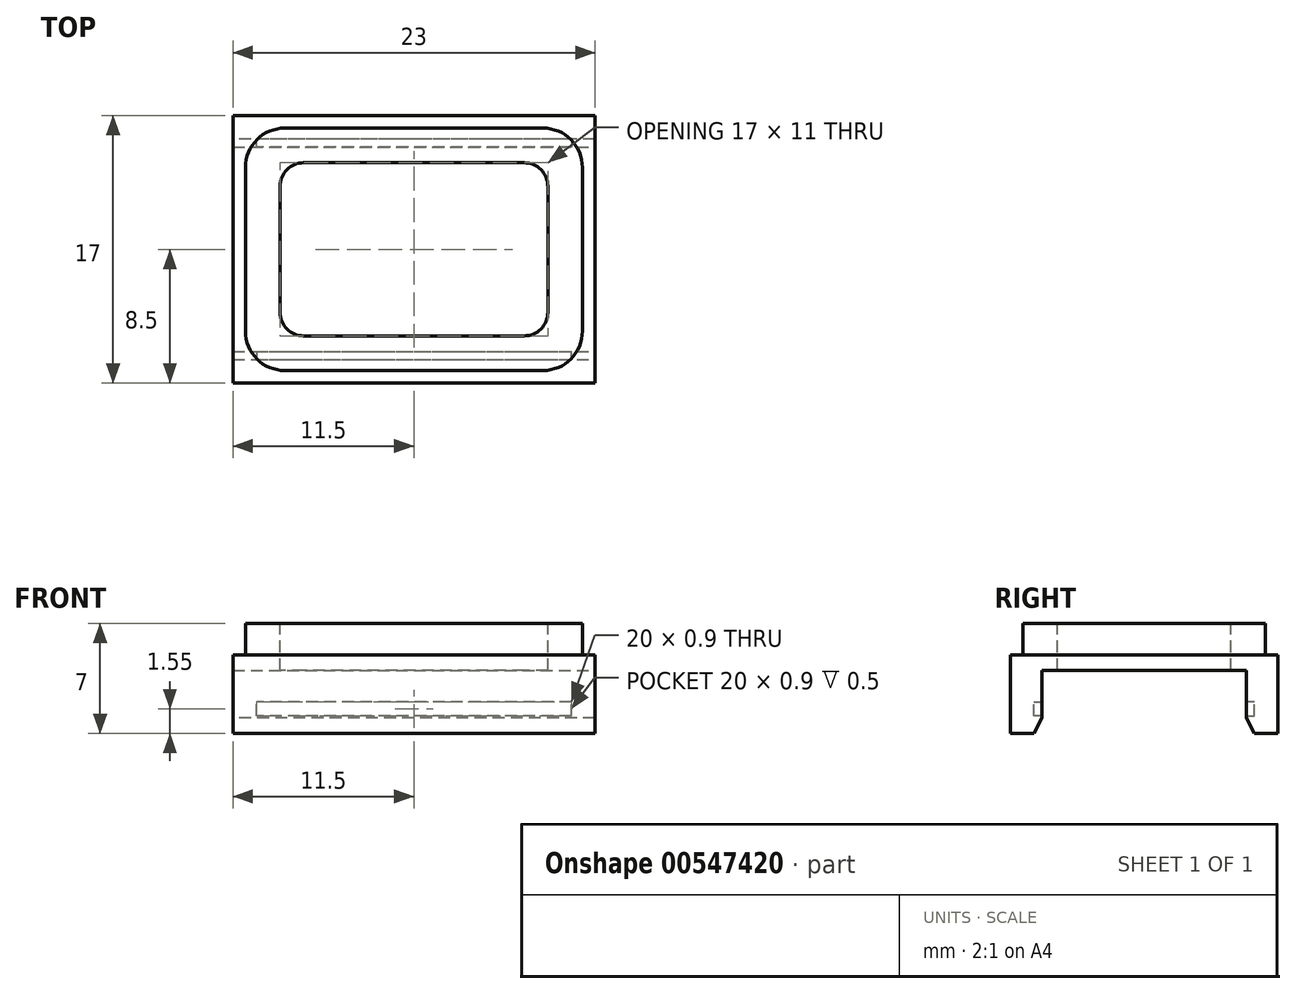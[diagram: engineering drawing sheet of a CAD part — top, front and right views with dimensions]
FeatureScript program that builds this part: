
annotation { "Feature Type Name" : "Feature", "Feature Type Description" : "" }
export const myFeature = defineFeature(function(context is Context, id is Id, definition is map)
    precondition{}
    {
        {
            var Q0;
            Q0=qCreatedBy(makeId("Top.planeOp"),FACE);
            var sketch = newSketch(context, id + "F0", { "sketchPlane" : qUnion([Q0])});
            skLineSegment(sketch, "E0.bottom", {"start": v(8.2, 7.7) * mm, "end": v(-8.2, 7.7) * mm});
            skLineSegment(sketch, "E0.top", {"start": v(8.2, -7.7) * mm, "end": v(-8.2, -7.7) * mm});
            skLineSegment(sketch, "E0.left", {"start": v(10.7, 5.2) * mm, "end": v(10.7, -5.2) * mm});
            skLineSegment(sketch, "E0.right", {"start": v(-10.7, 5.2) * mm, "end": v(-10.7, -5.2) * mm});
            skPoint(sketch, "E0.middle", {"position": v(0, 0) * mm});
            skPoint(sketch, "E1.visualSharp", {"position": v(-10.7, 7.7) * mm});
            skArc(sketch, "E1.filletArc", {"start": v(-8.2, 7.7) * mm, "mid": v(-9.97, 6.97) * mm, "end": v(-10.7, 5.2) * mm});
            skPoint(sketch, "E2.visualSharp", {"position": v(-10.7, -7.7) * mm});
            skArc(sketch, "E2.filletArc", {"start": v(-10.7, -5.2) * mm, "mid": v(-9.97, -6.97) * mm, "end": v(-8.2, -7.7) * mm});
            skPoint(sketch, "E3.visualSharp", {"position": v(10.7, 7.7) * mm});
            skArc(sketch, "E3.filletArc", {"start": v(10.7, 5.2) * mm, "mid": v(9.97, 6.97) * mm, "end": v(8.2, 7.7) * mm});
            skPoint(sketch, "E4.visualSharp", {"position": v(10.7, -7.7) * mm});
            skArc(sketch, "E4.filletArc", {"start": v(8.2, -7.7) * mm, "mid": v(9.97, -6.97) * mm, "end": v(10.7, -5.2) * mm});
            skLineSegment(sketch, "E5.bottom", {"start": v(11.5, 8.5) * mm, "end": v(-11.5, 8.5) * mm});
            skLineSegment(sketch, "E5.top", {"start": v(11.5, -8.5) * mm, "end": v(-11.5, -8.5) * mm});
            skLineSegment(sketch, "E5.left", {"start": v(11.5, 8.5) * mm, "end": v(11.5, -8.5) * mm});
            skLineSegment(sketch, "E5.right", {"start": v(-11.5, 8.5) * mm, "end": v(-11.5, -8.5) * mm});
            skSolve(sketch);
        }
        {
            var Q0;
            Q0=makeQuery(id+"F0.imprint","IMPRINT",FACE,{"disambiguationData":[TD([[makeQuery(id+"F0.imprint","IMPRINT",EDGE,{"derivedFrom":sQuery(id+"F0.wireOp",EDGE,"E0.bottom")}),-1.0]])]});
            extrude(context, id + "F1", {"entities" : qUnion([Q0]), "depth" : 1 * mm, "offsetDistance" : 25 * mm});
        }
        {
            var Q0;
            Q0=makeQuery(id+"F0.imprint","IMPRINT",FACE,{"disambiguationData":[TD([[makeQuery(id+"F0.imprint","IMPRINT",EDGE,{"derivedFrom":sQuery(id+"F0.wireOp",EDGE,"E0.bottom")}),1.0]])]});
            extrude(context, id + "F2", {"entities" : qUnion([Q0]), "operationType" : NewBodyOperationType.ADD, "depth" : 3 * mm, "offsetDistance" : 25 * mm});
        }
        {
            var Q0;
            Q0=makeQuery(id+"F0.imprint","IMPRINT",FACE,{"disambiguationData":[TD([[makeQuery(id+"F0.imprint","IMPRINT",EDGE,{"derivedFrom":sQuery(id+"F0.wireOp",EDGE,"E0.bottom")}),1.0]])]});
            var sketch = newSketch(context, id + "F3", { "sketchPlane" : qUnion([Q0])});
            skLineSegment(sketch, "E6.bottom", {"start": v(10, -7) * mm, "end": v(-10, -7) * mm});
            skLineSegment(sketch, "E6.left", {"start": v(10, -7) * mm, "end": v(10, -6.5) * mm});
            skLineSegment(sketch, "E6.right", {"start": v(-10, -7) * mm, "end": v(-10, -6.5) * mm});
            skPoint(sketch, "E6.middle", {"position": v(0, 0) * mm});
            skLineSegment(sketch, "E7", {"start": v(-10, -7) * mm, "end": v(-10, -8.5) * mm});
            skLineSegment(sketch, "E8", {"start": v(-10, -8.5) * mm, "end": v(10, -8.5) * mm});
            skLineSegment(sketch, "E9", {"start": v(10, -8.5) * mm, "end": v(10, -7) * mm});
            skLineSegment(sketch, "E10", {"start": v(-10, -6.5) * mm, "end": v(10, -6.5) * mm});
            skPoint(sketch, "E6.top.end.orphan", {"position": v(-10, 7) * mm});
            skPoint(sketch, "E11.orphan", {"position": v(10, 7) * mm});
            skLineSegment(sketch, "E12.MirrorCS", {"start": v(-10, 6.5) * mm, "end": v(10, 6.5) * mm});
            skLineSegment(sketch, "E13.MirrorCS", {"start": v(10, 7) * mm, "end": v(-10, 7) * mm});
            skLineSegment(sketch, "E14.MirrorCS", {"start": v(-10, 8.5) * mm, "end": v(10, 8.5) * mm});
            skLineSegment(sketch, "E15.MirrorCS", {"start": v(-10, 7) * mm, "end": v(-10, 8.5) * mm});
            skLineSegment(sketch, "E16.MirrorCS", {"start": v(10, 8.5) * mm, "end": v(10, 7) * mm});
            skLineSegment(sketch, "E17.MirrorCS", {"start": v(10, 7) * mm, "end": v(10, 6.5) * mm});
            skLineSegment(sketch, "E18.MirrorCS", {"start": v(-10, 7) * mm, "end": v(-10, 6.5) * mm});
            skSolve(sketch);
        }
        {
            var Q0;
            {var subQ4=sQuery(id+"F3.wireOp",EDGE,"E7");Q0=makeQuery(id+"F3.imprint","IMPRINT",FACE,{"disambiguationData":[TD([[makeQuery(id+"F3.imprint","IMPRINT",EDGE,{"derivedFrom":subQ4}),1.0]])]});}
            var Q1;
            {var subQ5=makeQuery(id+"F0.imprint","IMPRINT",EDGE,{"derivedFrom":sQuery(id+"F0.wireOp",EDGE,"E0.top")});Q1=makeQuery(id+"F3.imprint","IMPRINT",FACE,{"disambiguationData":[TD([[makeQuery(id+"F3.imprint","IMPRINT",EDGE,{"derivedFrom":subQ5}),-1.0]])]});}
            var Q2;
            Q2=makeQuery(id+"F3.imprint","IMPRINT",FACE,{"disambiguationData":[TD([[makeQuery(id+"F3.imprint","IMPRINT",EDGE,{"derivedFrom":sQuery(id+"F3.wireOp",EDGE,"E14.MirrorCS")}),-1.0]])]});
            var Q3;
            {var subQ5=makeQuery(id+"F0.imprint","IMPRINT",EDGE,{"derivedFrom":sQuery(id+"F0.wireOp",EDGE,"E0.bottom")});Q3=makeQuery(id+"F3.imprint","IMPRINT",FACE,{"disambiguationData":[TD([[makeQuery(id+"F3.imprint","IMPRINT",EDGE,{"derivedFrom":subQ5}),1.0]])]});}
            extrude(context, id + "F4", {"entities" : qUnion([Q0, Q1, Q2, Q3]), "operationType" : NewBodyOperationType.ADD, "oppositeDirection" : true, "depth" : 4 * mm, "offsetDistance" : 25 * mm});
        }
        {
            var Q0;
            {var subQ0=sQuery(id+"F3.wireOp",EDGE,"E10");Q0=makeQuery(id+"F3.imprint","IMPRINT",FACE,{"disambiguationData":[TD([[makeQuery(id+"F3.imprint","IMPRINT",EDGE,{"derivedFrom":subQ0}),-1.0]])]});}
            var Q1;
            {var subQ1=sQuery(id+"F3.wireOp",EDGE,"E12.MirrorCS");Q1=makeQuery(id+"F3.imprint","IMPRINT",FACE,{"disambiguationData":[TD([[makeQuery(id+"F3.imprint","IMPRINT",EDGE,{"derivedFrom":subQ1}),1.0]])]});}
            extrude(context, id + "F5", {"entities" : qUnion([Q0, Q1]), "operationType" : NewBodyOperationType.ADD, "oppositeDirection" : true, "depth" : 2 * mm, "offsetDistance" : 25 * mm});
        }
        {
            var Q0;
            {var subQ0=sQuery(id+"F3.wireOp",EDGE,"E6.left");var subQ3=makeQuery(id+"F0.imprint","IMPRINT",EDGE,{"derivedFrom":sQuery(id+"F0.wireOp",EDGE,"E4.filletArc")});var subQ5=makeQuery(id+"F3.imprint","INTERSECT",VERTEX,{"derivedFrom":[subQ3,subQ0]});Q0=makeQuery(id+"F3.imprint","IMPRINT",FACE,{"disambiguationData":[TD([[makeQuery(id+"F3.imprint","IMPRINT",EDGE,{"disambiguationData":[TD([[subQ5,1.0]])],"derivedFrom":subQ3}),-1.0]])]});}
            var Q1;
            {var subQ0=sQuery(id+"F3.wireOp",EDGE,"E17.MirrorCS");var subQ3=makeQuery(id+"F0.imprint","IMPRINT",EDGE,{"derivedFrom":sQuery(id+"F0.wireOp",EDGE,"E3.filletArc")});var subQ5=makeQuery(id+"F3.imprint","INTERSECT",VERTEX,{"derivedFrom":[subQ3,subQ0]});Q1=makeQuery(id+"F3.imprint","IMPRINT",FACE,{"disambiguationData":[TD([[makeQuery(id+"F3.imprint","IMPRINT",EDGE,{"disambiguationData":[TD([[subQ5,-1.0]])],"derivedFrom":subQ3}),-1.0]])]});}
            var Q2;
            {var subQ0=sQuery(id+"F3.wireOp",EDGE,"E18.MirrorCS");var subQ3=makeQuery(id+"F0.imprint","IMPRINT",EDGE,{"derivedFrom":sQuery(id+"F0.wireOp",EDGE,"E1.filletArc")});var subQ5=makeQuery(id+"F3.imprint","INTERSECT",VERTEX,{"derivedFrom":[subQ3,subQ0]});Q2=makeQuery(id+"F3.imprint","IMPRINT",FACE,{"disambiguationData":[TD([[makeQuery(id+"F3.imprint","IMPRINT",EDGE,{"disambiguationData":[TD([[subQ5,1.0]])],"derivedFrom":subQ3}),-1.0]])]});}
            var Q3;
            {var subQ0=sQuery(id+"F3.wireOp",EDGE,"E6.right");var subQ3=makeQuery(id+"F0.imprint","IMPRINT",EDGE,{"derivedFrom":sQuery(id+"F0.wireOp",EDGE,"E2.filletArc")});var subQ5=makeQuery(id+"F3.imprint","INTERSECT",VERTEX,{"derivedFrom":[subQ3,subQ0]});Q3=makeQuery(id+"F3.imprint","IMPRINT",FACE,{"disambiguationData":[TD([[makeQuery(id+"F3.imprint","IMPRINT",EDGE,{"disambiguationData":[TD([[subQ5,-1.0]])],"derivedFrom":subQ3}),-1.0]])]});}
            extrude(context, id + "F6", {"entities" : qUnion([Q0, Q1, Q2, Q3]), "operationType" : NewBodyOperationType.ADD, "oppositeDirection" : true, "depth" : 2 * mm, "offsetDistance" : 25 * mm});
        }
        {
            var Q0;
            {var subQ0=sQuery(id+"F0.wireOp",EDGE,"E4.filletArc");var subQ1=sQuery(id+"F0.wireOp",EDGE,"E3.filletArc");var subQ2=sQuery(id+"F0.wireOp",EDGE,"E2.filletArc");var subQ3=sQuery(id+"F0.wireOp",EDGE,"E1.filletArc");var subQ4=sQuery(id+"F0.wireOp",EDGE,"E0.right");var subQ5=sQuery(id+"F0.wireOp",EDGE,"E0.left");var subQ6=sQuery(id+"F0.wireOp",EDGE,"E0.top");var subQ7=sQuery(id+"F0.wireOp",EDGE,"E0.bottom");Q0=makeQuery(id+"F2.boolean.opBoolean","MERGE",FACE,{"derivedFrom":[makeQuery(id+"F1.opExtrude","CAP_FACE",FACE,{"disambiguationData":[OSD([subQ7,subQ6,subQ5,subQ4,subQ3,subQ2,subQ1,subQ0,sQuery(id+"F0.wireOp",EDGE,"E5.bottom"),sQuery(id+"F0.wireOp",EDGE,"E5.top"),sQuery(id+"F0.wireOp",EDGE,"E5.left"),sQuery(id+"F0.wireOp",EDGE,"E5.right")])],"isStart":true}),makeQuery(id+"F2.opExtrude","CAP_FACE",FACE,{"disambiguationData":[OSD([subQ7,subQ6,subQ5,subQ4,subQ3,subQ2,subQ1,subQ0])],"isStart":true})]});}
            var sketch = newSketch(context, id + "F7", { "sketchPlane" : qUnion([Q0])});
            skLineSegment(sketch, "E19", {"start": v(-10, 6.5) * mm, "end": v(-11.5, 6.5) * mm});
            skLineSegment(sketch, "E20", {"start": v(10, 6.5) * mm, "end": v(11.5, 6.5) * mm});
            skLineSegment(sketch, "E21.MirrorCS", {"start": v(-10, -6.5) * mm, "end": v(-11.5, -6.5) * mm});
            skLineSegment(sketch, "E22.MirrorCS", {"start": v(10, -6.5) * mm, "end": v(11.5, -6.5) * mm});
            skSolve(sketch);
        }
        {
            var Q0;
            {var subQ0=sQuery(id+"F7.wireOp",EDGE,"E20");Q0=makeQuery(id+"F7.imprint","IMPRINT",FACE,{"disambiguationData":[TD([[makeQuery(id+"F7.imprint","IMPRINT",EDGE,{"derivedFrom":subQ0}),1.0]])]});}
            var Q1;
            {var subQ0=sQuery(id+"F7.wireOp",EDGE,"E19");Q1=makeQuery(id+"F7.imprint","IMPRINT",FACE,{"disambiguationData":[TD([[makeQuery(id+"F7.imprint","IMPRINT",EDGE,{"derivedFrom":subQ0}),-1.0]])]});}
            var Q2;
            {var subQ0=sQuery(id+"F7.wireOp",EDGE,"E21.MirrorCS");Q2=makeQuery(id+"F7.imprint","IMPRINT",FACE,{"disambiguationData":[TD([[makeQuery(id+"F7.imprint","IMPRINT",EDGE,{"derivedFrom":subQ0}),1.0]])]});}
            var Q3;
            {var subQ0=sQuery(id+"F7.wireOp",EDGE,"E22.MirrorCS");Q3=makeQuery(id+"F7.imprint","IMPRINT",FACE,{"disambiguationData":[TD([[makeQuery(id+"F7.imprint","IMPRINT",EDGE,{"derivedFrom":subQ0}),-1.0]])]});}
            extrude(context, id + "F8", {"entities" : qUnion([Q0, Q1, Q2, Q3]), "operationType" : NewBodyOperationType.ADD, "depth" : 4 * mm, "offsetDistance" : 25 * mm});
        }
        {
            var Q0;
            Q0=makeQuery(id+"F4.opExtrude","SWEPT_FACE",FACE,{"disambiguationData":[OSD([sQuery(id+"F3.wireOp",EDGE,"E6.bottom")])]});
            var sketch = newSketch(context, id + "F9", { "sketchPlane" : qUnion([Q0])});
            skLineSegment(sketch, "E23", {"start": v(10, -2.9) * mm, "end": v(-10, -2.9) * mm});
            skPoint(sketch, "E23.endSnap0", {"position": v(-10, -3) * mm});
            skSolve(sketch);
        }
        {
            var Q0;
            {var subQ0=sQuery(id+"F9.wireOp",EDGE,"E23");Q0=makeQuery(id+"F9.imprint","IMPRINT",FACE,{"disambiguationData":[TD([[makeQuery(id+"F9.imprint","IMPRINT",EDGE,{"derivedFrom":subQ0}),1.0]])]});}
            extrude(context, id + "F10", {"entities" : qUnion([Q0]), "operationType" : NewBodyOperationType.ADD, "depth" : 0.5 * mm, "offsetDistance" : 25 * mm});
        }
        {
            var Q0;
            Q0=makeQuery(id+"F4.opExtrude","SWEPT_FACE",FACE,{"disambiguationData":[OSD([sQuery(id+"F3.wireOp",EDGE,"E13.MirrorCS")])]});
            var sketch = newSketch(context, id + "F11", { "sketchPlane" : qUnion([Q0])});
            skLineSegment(sketch, "E24", {"start": v(10, -2.9) * mm, "end": v(-10, -2.9) * mm});
            skSolve(sketch);
        }
        {
            var Q0;
            {var subQ0=sQuery(id+"F11.wireOp",EDGE,"E24");Q0=makeQuery(id+"F11.imprint","IMPRINT",FACE,{"disambiguationData":[TD([[makeQuery(id+"F11.imprint","IMPRINT",EDGE,{"derivedFrom":subQ0}),1.0]])]});}
            extrude(context, id + "F12", {"entities" : qUnion([Q0]), "operationType" : NewBodyOperationType.ADD, "depth" : 0.5 * mm, "offsetDistance" : 25 * mm});
        }
        {
            var Q0;
            Q0=makeQuery(id+"F12.boolean.opBoolean","MERGE",EDGE,{"derivedFrom":[makeQuery(id+"F8.opExtrude","CAP_EDGE",EDGE,{"disambiguationData":[OSD([sQuery(id+"F7.wireOp",EDGE,"E21.MirrorCS")])],"isStart":false}),makeQuery(id+"F8.opExtrude","CAP_EDGE",EDGE,{"disambiguationData":[OSD([sQuery(id+"F7.wireOp",EDGE,"E22.MirrorCS")])],"isStart":false}),makeQuery(id+"F12.opExtrude","CAP_EDGE",EDGE,{"disambiguationData":[OSD([sQuery(id+"F3.wireOp",EDGE,"E13.MirrorCS")])],"isStart":false})]});
            chamfer(context, id + "F13", {"entities" : qUnion([Q0]), "chamferType" : ChamferType.TWO_OFFSETS, "width1" : 0.5 * mm, "oppositeDirection" : false, "width2" : 1 * mm, "tangentPropagation" : true});
        }
        {
            var Q0;
            Q0=makeQuery(id+"F10.boolean.opBoolean","MERGE",EDGE,{"derivedFrom":[makeQuery(id+"F8.opExtrude","CAP_EDGE",EDGE,{"disambiguationData":[OSD([sQuery(id+"F7.wireOp",EDGE,"E19")])],"isStart":false}),makeQuery(id+"F8.opExtrude","CAP_EDGE",EDGE,{"disambiguationData":[OSD([sQuery(id+"F7.wireOp",EDGE,"E20")])],"isStart":false}),makeQuery(id+"F10.opExtrude","CAP_EDGE",EDGE,{"disambiguationData":[OSD([sQuery(id+"F3.wireOp",EDGE,"E6.bottom")])],"isStart":false})]});
            chamfer(context, id + "F14", {"entities" : qUnion([Q0]), "chamferType" : ChamferType.TWO_OFFSETS, "width1" : 1 * mm, "oppositeDirection" : false, "width2" : 0.5 * mm, "tangentPropagation" : true});
        }
        {
            var Q0;
            Q0=makeQuery(id+"F2.opExtrude","CAP_FACE",FACE,{"disambiguationData":[OSD([sQuery(id+"F0.wireOp",EDGE,"E0.bottom"),sQuery(id+"F0.wireOp",EDGE,"E0.top"),sQuery(id+"F0.wireOp",EDGE,"E0.left"),sQuery(id+"F0.wireOp",EDGE,"E0.right"),sQuery(id+"F0.wireOp",EDGE,"E1.filletArc"),sQuery(id+"F0.wireOp",EDGE,"E2.filletArc"),sQuery(id+"F0.wireOp",EDGE,"E3.filletArc"),sQuery(id+"F0.wireOp",EDGE,"E4.filletArc")])],"isStart":false});
            var sketch = newSketch(context, id + "F15", { "sketchPlane" : qUnion([Q0])});
            skLineSegment(sketch, "E25.bottom", {"start": v(8.5, 5.5) * mm, "end": v(-8.5, 5.5) * mm});
            skLineSegment(sketch, "E25.top", {"start": v(8.5, -5.5) * mm, "end": v(-8.5, -5.5) * mm});
            skLineSegment(sketch, "E25.left", {"start": v(8.5, 5.5) * mm, "end": v(8.5, -5.5) * mm});
            skLineSegment(sketch, "E25.right", {"start": v(-8.5, 5.5) * mm, "end": v(-8.5, -5.5) * mm});
            skPoint(sketch, "E25.middle", {"position": v(0, 0) * mm});
            skSolve(sketch);
        }
        {
            var Q0;
            Q0=makeQuery(id+"F15.imprint","IMPRINT",FACE,{"disambiguationData":[TD([[makeQuery(id+"F15.imprint","IMPRINT",EDGE,{"derivedFrom":sQuery(id+"F15.wireOp",EDGE,"E25.bottom")}),1.0]])]});
            extrude(context, id + "F16", {"entities" : qUnion([Q0]), "operationType" : NewBodyOperationType.REMOVE, "oppositeDirection" : true, "depth" : 25 * mm, "offsetDistance" : 25 * mm});
        }
        {
            var Q0;
            Q0=makeQuery(id+"F16.boolean.opBoolean","COPY",EDGE,{"derivedFrom":makeQuery(id+"F16.opExtrude","SWEPT_EDGE",EDGE,{"disambiguationData":[OSD([sQuery(id+"F15.wireOp",EDGE,"E25.top"),sQuery(id+"F15.wireOp",EDGE,"E25.right")])]})});
            var Q1;
            Q1=makeQuery(id+"F16.boolean.opBoolean","COPY",EDGE,{"derivedFrom":makeQuery(id+"F16.opExtrude","SWEPT_EDGE",EDGE,{"disambiguationData":[OSD([sQuery(id+"F15.wireOp",EDGE,"E25.bottom"),sQuery(id+"F15.wireOp",EDGE,"E25.right")])]})});
            var Q2;
            Q2=makeQuery(id+"F16.boolean.opBoolean","COPY",EDGE,{"derivedFrom":makeQuery(id+"F16.opExtrude","SWEPT_EDGE",EDGE,{"disambiguationData":[OSD([sQuery(id+"F15.wireOp",EDGE,"E25.bottom"),sQuery(id+"F15.wireOp",EDGE,"E25.left")])]})});
            var Q3;
            Q3=makeQuery(id+"F16.boolean.opBoolean","COPY",EDGE,{"derivedFrom":makeQuery(id+"F16.opExtrude","SWEPT_EDGE",EDGE,{"disambiguationData":[OSD([sQuery(id+"F15.wireOp",EDGE,"E25.top"),sQuery(id+"F15.wireOp",EDGE,"E25.left")])]})});
            fillet(context, id + "F17", {"entities" : qUnion([Q0, Q1, Q2, Q3]), "radius" : 1.5 * mm, "tangentPropagation" : true, "allowEdgeOverflow" : false});
        }
    });
